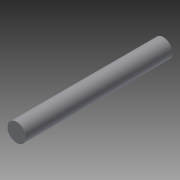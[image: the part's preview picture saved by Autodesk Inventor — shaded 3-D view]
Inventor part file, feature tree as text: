
AUTODESK INVENTOR PART (.ipt)
format: ipt  version: 2014 (Build 180170000, 170)  size: 68,608 bytes
history: native  units: in
note: dims shown in document units (in); Inventor stores cm internally (conversion verified against a paired STEP export)
features: extrude x1, sketch x1
ambient origin geometry x8: Origin, YZ Plane, XZ Plane, XY Plane, X Axis, Y Axis, Z Axis, Center Point
bodies: Solid1 (feature_tree)
feature tree (2):
  extrude  "Extrusion1"  Depth=2.0in TaperAngle=0.0deg
  sketch  "Sketch1"  dims[d0=0.25in d1=2.0in d2=0.0in]
